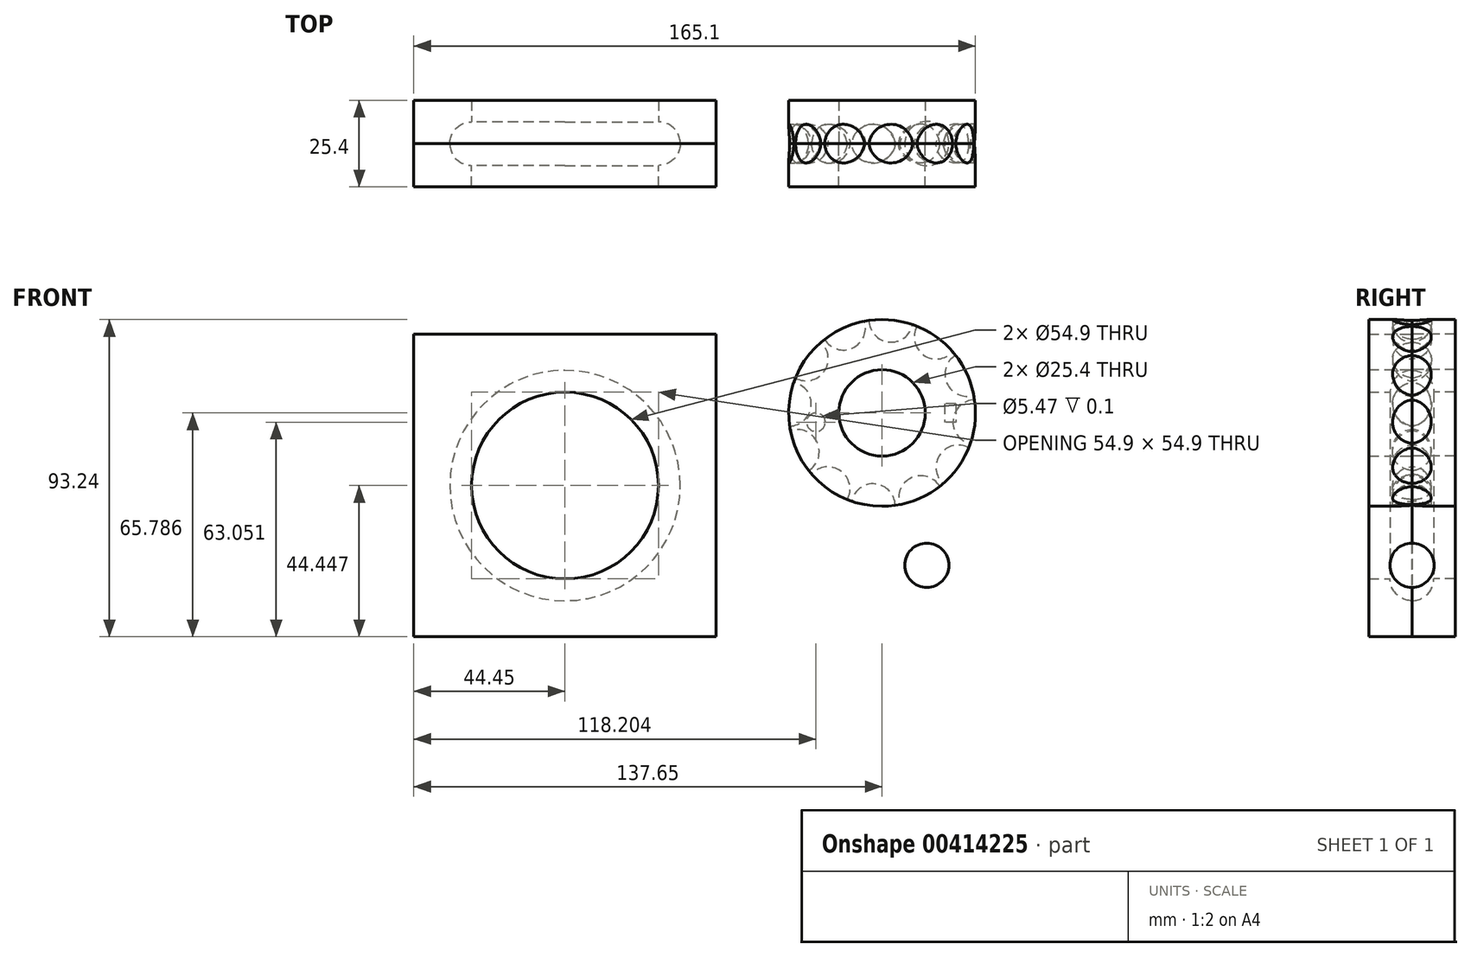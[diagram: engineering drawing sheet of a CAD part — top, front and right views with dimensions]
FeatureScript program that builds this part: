
annotation { "Feature Type Name" : "Feature", "Feature Type Description" : "" }
export const myFeature = defineFeature(function(context is Context, id is Id, definition is map)
    precondition{}
    {
        {
            var Q0;
            Q0=qCreatedBy(makeId("Front.planeOp"),FACE);
            var sketch = newSketch(context, id + "F0", { "sketchPlane" : qUnion([Q0])});
            skArc(sketch, "E0", {"start": v(0, -6.5) * mm, "mid": v(6.5, 0) * mm, "end": v(0, 6.5) * mm});
            skLineSegment(sketch, "E1", {"start": v(0, 6.5) * mm, "end": v(0, -6.5) * mm, "construction": true});
            skLineSegment(sketch, "E2", {"start": v(0, 6.5) * mm, "end": v(0, -6.5) * mm});
            skSolve(sketch);
        }
        {
            var Q0;
            Q0=makeQuery(id+"F0.imprint","IMPRINT",FACE,{"disambiguationData":[TD([[makeQuery(id+"F0.imprint","IMPRINT",EDGE,{"derivedFrom":sQuery(id+"F0.wireOp",EDGE,"E0")}),1.0]])]});
            var Q1;
            Q1=sQuery(id+"F0.wireOp",EDGE,"E2");
            revolve(context, id + "F1", {"entities" : qUnion([Q0]), "axis" : qUnion([Q1]), "revolveType" : RevolveType.FULL});
        }
        {
            var Q0;
            Q0=qCreatedBy(makeId("Front.planeOp"),FACE);
            var sketch = newSketch(context, id + "F2", { "sketchPlane" : qUnion([Q0])});
            skLineSegment(sketch, "E3.bottom", {"start": v(-150.8, 67.89) * mm, "end": v(-61.9, 67.89) * mm});
            skLineSegment(sketch, "E3.top", {"start": v(-150.8, -21.01) * mm, "end": v(-61.9, -21.01) * mm});
            skLineSegment(sketch, "E3.left", {"start": v(-150.8, 67.89) * mm, "end": v(-150.8, -21.01) * mm});
            skLineSegment(sketch, "E3.right", {"start": v(-61.9, 67.89) * mm, "end": v(-61.9, -21.01) * mm});
            skLineSegment(sketch, "E4", {"start": v(-106.35, 67.89) * mm, "end": v(-106.35, -21.01) * mm, "construction": true});
            skCircle(sketch, "E5", {"center": v(-106.35, 23.44) * mm, "radius": 20.95 * mm});
            skCircle(sketch, "E6.0", {"center": v(-106.35, 23.44) * mm, "radius": 27.45 * mm});
            skSolve(sketch);
        }
        {
            var Q0;
            Q0=sQuery(id+"F2.wireOp",EDGE,"E6.0");
            cPlane(context, id + "F3", {"entities" : qUnion([Q0]), "cplaneType" : CPlaneType.LINE_ANGLE, "offset" : 25 * mm, "angle" : 0 * degree, "width" : 150 * mm, "height" : 150 * mm});
        }
        {
            var Q0;
            Q0=qCreatedBy(id+"F3.planeOp",FACE);
            var sketch = newSketch(context, id + "F4", { "sketchPlane" : qUnion([Q0])});
            skCircle(sketch, "E7", {"center": v(-133.8, 0) * mm, "radius": 6.4 * mm});
            skSolve(sketch);
        }
        {
            var Q0;
            Q0=makeQuery(id+"F2.imprint","IMPRINT",FACE,{"disambiguationData":[TD([[makeQuery(id+"F2.imprint","IMPRINT",EDGE,{"derivedFrom":sQuery(id+"F2.wireOp",EDGE,"E3.bottom")}),-1.0]])]});
            extrude(context, id + "F5", {"entities" : qUnion([Q0]), "depth" : 12.7 * mm});
        }
        {
            var Q0;
            Q0=makeQuery(id+"F4.imprint","IMPRINT",FACE,{"disambiguationData":[TD([[makeQuery(id+"F4.imprint","IMPRINT",EDGE,{"derivedFrom":sQuery(id+"F4.wireOp",EDGE,"E7")}),1.0]])]});
            var Q1;
            Q1=sQuery(id+"F2.wireOp",EDGE,"E6.0");
            revolve(context, id + "F6", {"operationType" : NewBodyOperationType.REMOVE, "entities" : qUnion([Q0]), "axis" : qUnion([Q1]), "revolveType" : RevolveType.FULL, "oppositeDirection" : true});
        }
        {
            var Q0;
            Q0=qCreatedBy(makeId("Front.planeOp"),FACE);
            var sketch = newSketch(context, id + "F7", { "sketchPlane" : qUnion([Q0])});
            skCircle(sketch, "E8", {"center": v(-13.15, 44.78) * mm, "radius": 12.7 * mm});
            skCircle(sketch, "E9", {"center": v(-13.15, 44.78) * mm, "radius": 27.45 * mm});
            skArc(sketch, "E10", {"start": v(14.03, 48.64) * mm, "mid": v(7.7, 42.76) * mm, "end": v(12.79, 35.79) * mm});
            skLineSegment(sketch, "E11", {"start": v(14.17, 42.14) * mm, "end": v(7.7, 42.76) * mm, "construction": true});
            skLineSegment(sketch, "E12", {"start": v(7.7, 42.76) * mm, "end": v(14.17, 42.14) * mm});
            skLineSegment(sketch, "E13", {"start": v(14.03, 48.64) * mm, "end": v(12.79, 35.79) * mm});
            skArc(sketch, "E14.1.0", {"start": v(8.46, 61.7) * mm, "mid": v(5.92, 53.46) * mm, "end": v(13.8, 49.96) * mm});
            skLineSegment(sketch, "E14.1.1", {"start": v(8.46, 61.7) * mm, "end": v(13.8, 49.96) * mm});
            skArc(sketch, "E14.2.0", {"start": v(-2.9, 70.24) * mm, "mid": v(-0.98, 61.83) * mm, "end": v(7.6, 62.74) * mm});
            skLineSegment(sketch, "E14.2.1", {"start": v(-2.9, 70.24) * mm, "end": v(7.6, 62.74) * mm});
            skArc(sketch, "E14.3.0", {"start": v(-17, 71.95) * mm, "mid": v(-11.14, 65.63) * mm, "end": v(-4.16, 70.71) * mm});
            skLineSegment(sketch, "E14.3.1", {"start": v(-17, 71.95) * mm, "end": v(-4.16, 70.71) * mm});
            skArc(sketch, "E14.4.0", {"start": v(-30.08, 66.38) * mm, "mid": v(-21.83, 63.84) * mm, "end": v(-18.33, 71.73) * mm});
            skLineSegment(sketch, "E14.4.1", {"start": v(-30.08, 66.38) * mm, "end": v(-18.33, 71.73) * mm});
            skArc(sketch, "E14.5.0", {"start": v(-38.62, 55.02) * mm, "mid": v(-30.2, 56.95) * mm, "end": v(-31.12, 65.53) * mm});
            skLineSegment(sketch, "E14.5.1", {"start": v(-38.62, 55.02) * mm, "end": v(-31.12, 65.53) * mm});
            skArc(sketch, "E14.6.0", {"start": v(-40.33, 40.92) * mm, "mid": v(-34, 46.79) * mm, "end": v(-39.09, 53.77) * mm});
            skLineSegment(sketch, "E14.6.1", {"start": v(-40.33, 40.92) * mm, "end": v(-39.09, 53.77) * mm});
            skArc(sketch, "E14.7.0", {"start": v(-34.76, 27.84) * mm, "mid": v(-32.22, 36.1) * mm, "end": v(-40.1, 39.6) * mm});
            skLineSegment(sketch, "E14.7.1", {"start": v(-34.76, 27.84) * mm, "end": v(-40.1, 39.6) * mm});
            skArc(sketch, "E14.8.0", {"start": v(-23.4, 19.3) * mm, "mid": v(-25.32, 27.72) * mm, "end": v(-33.9, 26.8) * mm});
            skLineSegment(sketch, "E14.8.1", {"start": v(-23.4, 19.3) * mm, "end": v(-33.9, 26.8) * mm});
            skArc(sketch, "E14.9.0", {"start": v(-9.3, 17.6) * mm, "mid": v(-15.16, 23.92) * mm, "end": v(-22.14, 18.84) * mm});
            skLineSegment(sketch, "E14.9.1", {"start": v(-9.3, 17.6) * mm, "end": v(-22.14, 18.84) * mm});
            skArc(sketch, "E14.10.0", {"start": v(3.78, 23.17) * mm, "mid": v(-4.47, 25.7) * mm, "end": v(-7.97, 17.82) * mm});
            skLineSegment(sketch, "E14.10.1", {"start": v(3.78, 23.17) * mm, "end": v(-7.97, 17.82) * mm});
            skArc(sketch, "E14.11.0", {"start": v(12.32, 34.53) * mm, "mid": v(3.9, 32.6) * mm, "end": v(4.82, 24.02) * mm});
            skLineSegment(sketch, "E14.11.1", {"start": v(12.32, 34.53) * mm, "end": v(4.82, 24.02) * mm});
            skSolve(sketch);
        }
        {
            var Q0;
            {var subQ0=sQuery(id+"F7.wireOp",EDGE,"E10");Q0=makeQuery(id+"F7.imprint","IMPRINT",FACE,{"disambiguationData":[TD([[makeQuery(id+"F7.imprint","IMPRINT",EDGE,{"derivedFrom":subQ0}),1.0]])]});}
            var Q1;
            {var subQ1=sQuery(id+"F7.wireOp",EDGE,"E9");var subQ3=sQuery(id+"F7.wireOp",EDGE,"E12");var subQ4=makeQuery(id+"F7.imprint","INTERSECT",VERTEX,{"derivedFrom":[subQ1,subQ3]});Q1=makeQuery(id+"F7.imprint","IMPRINT",FACE,{"disambiguationData":[TD([[makeQuery(id+"F7.imprint","IMPRINT",EDGE,{"disambiguationData":[TD([[subQ4,1.0]])],"derivedFrom":subQ3}),1.0]])]});}
            var Q2;
            {var subQ1=sQuery(id+"F7.wireOp",EDGE,"E9");var subQ3=sQuery(id+"F7.wireOp",EDGE,"E12");var subQ4=makeQuery(id+"F7.imprint","INTERSECT",VERTEX,{"derivedFrom":[subQ1,subQ3]});Q2=makeQuery(id+"F7.imprint","IMPRINT",FACE,{"disambiguationData":[TD([[makeQuery(id+"F7.imprint","IMPRINT",EDGE,{"disambiguationData":[TD([[subQ4,1.0]])],"derivedFrom":subQ3}),-1.0]])]});}
            var Q3;
            {var subQ0=sQuery(id+"F7.wireOp",EDGE,"E14.1.1");Q3=makeQuery(id+"F7.imprint","IMPRINT",FACE,{"disambiguationData":[TD([[makeQuery(id+"F7.imprint","IMPRINT",EDGE,{"derivedFrom":subQ0}),1.0]])]});}
            var Q4;
            {var subQ0=sQuery(id+"F7.wireOp",EDGE,"E14.2.1");Q4=makeQuery(id+"F7.imprint","IMPRINT",FACE,{"disambiguationData":[TD([[makeQuery(id+"F7.imprint","IMPRINT",EDGE,{"derivedFrom":subQ0}),1.0]])]});}
            var Q5;
            Q5=makeQuery(id+"F7.imprint","IMPRINT",FACE,{"disambiguationData":[TD([[makeQuery(id+"F7.imprint","IMPRINT",EDGE,{"derivedFrom":sQuery(id+"F7.wireOp",EDGE,"E14.1.0")}),1.0]])]});
            var Q6;
            Q6=makeQuery(id+"F7.imprint","IMPRINT",FACE,{"disambiguationData":[TD([[makeQuery(id+"F7.imprint","IMPRINT",EDGE,{"derivedFrom":sQuery(id+"F7.wireOp",EDGE,"E14.2.0")}),1.0]])]});
            var Q7;
            Q7=makeQuery(id+"F7.imprint","IMPRINT",FACE,{"disambiguationData":[TD([[makeQuery(id+"F7.imprint","IMPRINT",EDGE,{"derivedFrom":sQuery(id+"F7.wireOp",EDGE,"E14.3.0")}),1.0]])]});
            var Q8;
            Q8=makeQuery(id+"F7.imprint","IMPRINT",FACE,{"disambiguationData":[TD([[makeQuery(id+"F7.imprint","IMPRINT",EDGE,{"derivedFrom":sQuery(id+"F7.wireOp",EDGE,"E14.4.0")}),1.0]])]});
            var Q9;
            Q9=makeQuery(id+"F7.imprint","IMPRINT",FACE,{"disambiguationData":[TD([[makeQuery(id+"F7.imprint","IMPRINT",EDGE,{"derivedFrom":sQuery(id+"F7.wireOp",EDGE,"E14.5.0")}),1.0]])]});
            var Q10;
            Q10=makeQuery(id+"F7.imprint","IMPRINT",FACE,{"disambiguationData":[TD([[makeQuery(id+"F7.imprint","IMPRINT",EDGE,{"derivedFrom":sQuery(id+"F7.wireOp",EDGE,"E8")}),-1.0]])]});
            var Q11;
            Q11=makeQuery(id+"F7.imprint","IMPRINT",FACE,{"disambiguationData":[TD([[makeQuery(id+"F7.imprint","IMPRINT",EDGE,{"derivedFrom":sQuery(id+"F7.wireOp",EDGE,"E14.11.0")}),1.0]])]});
            var Q12;
            Q12=makeQuery(id+"F7.imprint","IMPRINT",FACE,{"disambiguationData":[TD([[makeQuery(id+"F7.imprint","IMPRINT",EDGE,{"derivedFrom":sQuery(id+"F7.wireOp",EDGE,"E14.10.0")}),1.0]])]});
            var Q13;
            Q13=makeQuery(id+"F7.imprint","IMPRINT",FACE,{"disambiguationData":[TD([[makeQuery(id+"F7.imprint","IMPRINT",EDGE,{"derivedFrom":sQuery(id+"F7.wireOp",EDGE,"E14.9.0")}),1.0]])]});
            var Q14;
            Q14=makeQuery(id+"F7.imprint","IMPRINT",FACE,{"disambiguationData":[TD([[makeQuery(id+"F7.imprint","IMPRINT",EDGE,{"derivedFrom":sQuery(id+"F7.wireOp",EDGE,"E14.8.0")}),1.0]])]});
            var Q15;
            Q15=makeQuery(id+"F7.imprint","IMPRINT",FACE,{"disambiguationData":[TD([[makeQuery(id+"F7.imprint","IMPRINT",EDGE,{"derivedFrom":sQuery(id+"F7.wireOp",EDGE,"E14.7.0")}),1.0]])]});
            var Q16;
            Q16=makeQuery(id+"F7.imprint","IMPRINT",FACE,{"disambiguationData":[TD([[makeQuery(id+"F7.imprint","IMPRINT",EDGE,{"derivedFrom":sQuery(id+"F7.wireOp",EDGE,"E14.6.0")}),1.0]])]});
            var Q17;
            {var subQ0=sQuery(id+"F7.wireOp",EDGE,"E14.4.1");Q17=makeQuery(id+"F7.imprint","IMPRINT",FACE,{"disambiguationData":[TD([[makeQuery(id+"F7.imprint","IMPRINT",EDGE,{"derivedFrom":subQ0}),1.0]])]});}
            var Q18;
            {var subQ0=sQuery(id+"F7.wireOp",EDGE,"E14.5.1");Q18=makeQuery(id+"F7.imprint","IMPRINT",FACE,{"disambiguationData":[TD([[makeQuery(id+"F7.imprint","IMPRINT",EDGE,{"derivedFrom":subQ0}),1.0]])]});}
            var Q19;
            {var subQ0=sQuery(id+"F7.wireOp",EDGE,"E14.3.1");Q19=makeQuery(id+"F7.imprint","IMPRINT",FACE,{"disambiguationData":[TD([[makeQuery(id+"F7.imprint","IMPRINT",EDGE,{"derivedFrom":subQ0}),1.0]])]});}
            var Q20;
            {var subQ0=sQuery(id+"F7.wireOp",EDGE,"E14.6.1");Q20=makeQuery(id+"F7.imprint","IMPRINT",FACE,{"disambiguationData":[TD([[makeQuery(id+"F7.imprint","IMPRINT",EDGE,{"derivedFrom":subQ0}),1.0]])]});}
            var Q21;
            {var subQ0=sQuery(id+"F7.wireOp",EDGE,"E14.7.1");Q21=makeQuery(id+"F7.imprint","IMPRINT",FACE,{"disambiguationData":[TD([[makeQuery(id+"F7.imprint","IMPRINT",EDGE,{"derivedFrom":subQ0}),1.0]])]});}
            var Q22;
            {var subQ0=sQuery(id+"F7.wireOp",EDGE,"E14.8.1");Q22=makeQuery(id+"F7.imprint","IMPRINT",FACE,{"disambiguationData":[TD([[makeQuery(id+"F7.imprint","IMPRINT",EDGE,{"derivedFrom":subQ0}),1.0]])]});}
            var Q23;
            {var subQ0=sQuery(id+"F7.wireOp",EDGE,"E14.9.1");Q23=makeQuery(id+"F7.imprint","IMPRINT",FACE,{"disambiguationData":[TD([[makeQuery(id+"F7.imprint","IMPRINT",EDGE,{"derivedFrom":subQ0}),1.0]])]});}
            var Q24;
            {var subQ0=sQuery(id+"F7.wireOp",EDGE,"E14.10.1");Q24=makeQuery(id+"F7.imprint","IMPRINT",FACE,{"disambiguationData":[TD([[makeQuery(id+"F7.imprint","IMPRINT",EDGE,{"derivedFrom":subQ0}),1.0]])]});}
            var Q25;
            {var subQ0=sQuery(id+"F7.wireOp",EDGE,"E14.11.1");Q25=makeQuery(id+"F7.imprint","IMPRINT",FACE,{"disambiguationData":[TD([[makeQuery(id+"F7.imprint","IMPRINT",EDGE,{"derivedFrom":subQ0}),1.0]])]});}
            extrude(context, id + "F8", {"entities" : qUnion([Q0, Q1, Q2, Q3, Q4, Q5, Q6, Q7, Q8, Q9, Q10, Q11, Q12, Q13, Q14, Q15, Q16, Q17, Q18, Q19, Q20, Q21, Q22, Q23, Q24, Q25]), "depth" : 12.7 * mm});
        }
        {
            var Q0;
            {var subQ1=sQuery(id+"F7.wireOp",EDGE,"E10");var subQ3=sQuery(id+"F7.wireOp",EDGE,"E12");var subQ4=makeQuery(id+"F7.imprint","INTERSECT",VERTEX,{"derivedFrom":[subQ1,subQ3]});Q0=makeQuery(id+"F7.imprint","IMPRINT",FACE,{"disambiguationData":[TD([[makeQuery(id+"F7.imprint","IMPRINT",EDGE,{"disambiguationData":[TD([[subQ4,-1.0]])],"derivedFrom":subQ3}),1.0]])]});}
            var Q1;
            {var subQ1=sQuery(id+"F7.wireOp",EDGE,"E10");var subQ3=sQuery(id+"F7.wireOp",EDGE,"E12");var subQ4=makeQuery(id+"F7.imprint","INTERSECT",VERTEX,{"derivedFrom":[subQ1,subQ3]});Q1=makeQuery(id+"F7.imprint","IMPRINT",FACE,{"disambiguationData":[TD([[makeQuery(id+"F7.imprint","IMPRINT",EDGE,{"disambiguationData":[TD([[subQ4,-1.0]])],"derivedFrom":subQ3}),-1.0]])]});}
            var Q2;
            Q2=sQuery(id+"F7.wireOp",EDGE,"E13");
            revolve(context, id + "F9", {"operationType" : NewBodyOperationType.REMOVE, "entities" : qUnion([Q0, Q1]), "axis" : qUnion([Q2]), "revolveType" : RevolveType.FULL, "oppositeDirection" : true});
        }
        {
            var Q0;
            Q0=makeQuery(id+"F7.imprint","IMPRINT",FACE,{"disambiguationData":[TD([[makeQuery(id+"F7.imprint","IMPRINT",EDGE,{"derivedFrom":sQuery(id+"F7.wireOp",EDGE,"E14.1.0")}),1.0]])]});
            var Q1;
            Q1=sQuery(id+"F7.wireOp",EDGE,"E14.1.1");
            revolve(context, id + "F10", {"operationType" : NewBodyOperationType.REMOVE, "entities" : qUnion([Q0]), "axis" : qUnion([Q1]), "revolveType" : RevolveType.FULL, "oppositeDirection" : true});
        }
        {
            var Q0;
            Q0=makeQuery(id+"F7.imprint","IMPRINT",FACE,{"disambiguationData":[TD([[makeQuery(id+"F7.imprint","IMPRINT",EDGE,{"derivedFrom":sQuery(id+"F7.wireOp",EDGE,"E14.2.0")}),1.0]])]});
            var Q1;
            Q1=sQuery(id+"F7.wireOp",EDGE,"E14.2.1");
            revolve(context, id + "F11", {"operationType" : NewBodyOperationType.REMOVE, "entities" : qUnion([Q0]), "axis" : qUnion([Q1]), "revolveType" : RevolveType.FULL, "oppositeDirection" : true});
        }
        {
            var Q0;
            Q0=makeQuery(id+"F7.imprint","IMPRINT",FACE,{"disambiguationData":[TD([[makeQuery(id+"F7.imprint","IMPRINT",EDGE,{"derivedFrom":sQuery(id+"F7.wireOp",EDGE,"E14.3.0")}),1.0]])]});
            var Q1;
            Q1=sQuery(id+"F7.wireOp",EDGE,"E14.3.1");
            revolve(context, id + "F12", {"operationType" : NewBodyOperationType.REMOVE, "entities" : qUnion([Q0]), "axis" : qUnion([Q1]), "revolveType" : RevolveType.FULL, "oppositeDirection" : true});
        }
        {
            var Q0;
            Q0=makeQuery(id+"F7.imprint","IMPRINT",FACE,{"disambiguationData":[TD([[makeQuery(id+"F7.imprint","IMPRINT",EDGE,{"derivedFrom":sQuery(id+"F7.wireOp",EDGE,"E14.4.0")}),1.0]])]});
            var Q1;
            Q1=sQuery(id+"F7.wireOp",EDGE,"E14.4.1");
            revolve(context, id + "F13", {"operationType" : NewBodyOperationType.REMOVE, "entities" : qUnion([Q0]), "axis" : qUnion([Q1]), "revolveType" : RevolveType.FULL, "oppositeDirection" : true});
        }
        {
            var Q0;
            Q0=makeQuery(id+"F7.imprint","IMPRINT",FACE,{"disambiguationData":[TD([[makeQuery(id+"F7.imprint","IMPRINT",EDGE,{"derivedFrom":sQuery(id+"F7.wireOp",EDGE,"E14.5.0")}),1.0]])]});
            var Q1;
            Q1=sQuery(id+"F7.wireOp",EDGE,"E14.5.1");
            revolve(context, id + "F14", {"operationType" : NewBodyOperationType.REMOVE, "entities" : qUnion([Q0]), "axis" : qUnion([Q1]), "revolveType" : RevolveType.FULL, "oppositeDirection" : true});
        }
        {
            var Q0;
            Q0=makeQuery(id+"F7.imprint","IMPRINT",FACE,{"disambiguationData":[TD([[makeQuery(id+"F7.imprint","IMPRINT",EDGE,{"derivedFrom":sQuery(id+"F7.wireOp",EDGE,"E14.6.0")}),1.0]])]});
            var Q1;
            Q1=sQuery(id+"F7.wireOp",EDGE,"E14.6.1");
            revolve(context, id + "F15", {"operationType" : NewBodyOperationType.REMOVE, "entities" : qUnion([Q0]), "axis" : qUnion([Q1]), "revolveType" : RevolveType.FULL, "oppositeDirection" : true});
        }
        {
            var Q0;
            Q0=makeQuery(id+"F7.imprint","IMPRINT",FACE,{"disambiguationData":[TD([[makeQuery(id+"F7.imprint","IMPRINT",EDGE,{"derivedFrom":sQuery(id+"F7.wireOp",EDGE,"E14.7.0")}),1.0]])]});
            var Q1;
            Q1=sQuery(id+"F7.wireOp",EDGE,"E14.7.1");
            revolve(context, id + "F16", {"operationType" : NewBodyOperationType.REMOVE, "entities" : qUnion([Q0]), "axis" : qUnion([Q1]), "revolveType" : RevolveType.FULL, "oppositeDirection" : true});
        }
        {
            var Q0;
            Q0=makeQuery(id+"F7.imprint","IMPRINT",FACE,{"disambiguationData":[TD([[makeQuery(id+"F7.imprint","IMPRINT",EDGE,{"derivedFrom":sQuery(id+"F7.wireOp",EDGE,"E14.8.0")}),1.0]])]});
            var Q1;
            Q1=sQuery(id+"F7.wireOp",EDGE,"E14.8.1");
            revolve(context, id + "F17", {"operationType" : NewBodyOperationType.REMOVE, "entities" : qUnion([Q0]), "axis" : qUnion([Q1]), "revolveType" : RevolveType.FULL, "oppositeDirection" : true});
        }
        {
            var Q0;
            Q0=makeQuery(id+"F7.imprint","IMPRINT",FACE,{"disambiguationData":[TD([[makeQuery(id+"F7.imprint","IMPRINT",EDGE,{"derivedFrom":sQuery(id+"F7.wireOp",EDGE,"E14.9.0")}),1.0]])]});
            var Q1;
            Q1=sQuery(id+"F7.wireOp",EDGE,"E14.9.1");
            revolve(context, id + "F18", {"operationType" : NewBodyOperationType.REMOVE, "entities" : qUnion([Q0]), "axis" : qUnion([Q1]), "revolveType" : RevolveType.FULL, "oppositeDirection" : true});
        }
        {
            var Q0;
            Q0=makeQuery(id+"F7.imprint","IMPRINT",FACE,{"disambiguationData":[TD([[makeQuery(id+"F7.imprint","IMPRINT",EDGE,{"derivedFrom":sQuery(id+"F7.wireOp",EDGE,"E14.10.0")}),1.0]])]});
            var Q1;
            Q1=sQuery(id+"F7.wireOp",EDGE,"E14.10.1");
            revolve(context, id + "F19", {"operationType" : NewBodyOperationType.REMOVE, "entities" : qUnion([Q0]), "axis" : qUnion([Q1]), "revolveType" : RevolveType.FULL, "oppositeDirection" : true});
        }
        {
            var Q0;
            Q0=makeQuery(id+"F7.imprint","IMPRINT",FACE,{"disambiguationData":[TD([[makeQuery(id+"F7.imprint","IMPRINT",EDGE,{"derivedFrom":sQuery(id+"F7.wireOp",EDGE,"E14.11.0")}),1.0]])]});
            var Q1;
            Q1=sQuery(id+"F7.wireOp",EDGE,"E14.11.1");
            revolve(context, id + "F20", {"operationType" : NewBodyOperationType.REMOVE, "entities" : qUnion([Q0]), "axis" : qUnion([Q1]), "revolveType" : RevolveType.FULL, "oppositeDirection" : true});
        }
        {
            var Q0;
            Q0=makeQuery(id+"F8.opExtrude","SWEPT_BODY",BODY,{"disambiguationData":[OSD([sQuery(id+"F7.wireOp",EDGE,"E8"),sQuery(id+"F7.wireOp",EDGE,"E9")])]});
            var Q1;
            Q1=makeQuery(id+"F8.opExtrude","CAP_FACE",FACE,{"disambiguationData":[OSD([sQuery(id+"F7.wireOp",EDGE,"E8"),sQuery(id+"F7.wireOp",EDGE,"E9")])],"isStart":true});
            mirror(context, id + "F21", {"operationType" : NewBodyOperationType.ADD, "entities" : qUnion([Q0]), "mirrorPlane" : qUnion([Q1])});
        }
        {
            var Q0;
            Q0=makeQuery(id+"F21.opPattern","COPY",FACE,{"derivedFrom":makeQuery(id+"F8.opExtrude","CAP_FACE",FACE,{"disambiguationData":[OSD([sQuery(id+"F7.wireOp",EDGE,"E8"),sQuery(id+"F7.wireOp",EDGE,"E9")])],"isStart":false}),"instanceName":"1"});
            var sketch = newSketch(context, id + "F22", { "sketchPlane" : qUnion([Q0])});
            skCircle(sketch, "E15", {"center": v(32.6, 42.04) * mm, "radius": 2.73 * mm});
            skLineSegment(sketch, "E16.bottom", {"start": v(-8.55, 47.43) * mm, "end": v(-5.27, 47.43) * mm});
            skLineSegment(sketch, "E16.top", {"start": v(-8.55, 42) * mm, "end": v(-5.27, 42) * mm});
            skLineSegment(sketch, "E16.left", {"start": v(-8.55, 47.43) * mm, "end": v(-8.55, 42) * mm});
            skLineSegment(sketch, "E16.right", {"start": v(-5.27, 47.43) * mm, "end": v(-5.27, 42) * mm});
            skSolve(sketch);
        }
        {
            var Q0;
            Q0=makeQuery(id+"F22.imprint","IMPRINT",FACE,{"disambiguationData":[TD([[makeQuery(id+"F22.imprint","IMPRINT",EDGE,{"derivedFrom":sQuery(id+"F22.wireOp",EDGE,"E16.bottom")}),-1.0]])]});
            extrude(context, id + "F23", {"entities" : qUnion([Q0]), "operationType" : NewBodyOperationType.REMOVE, "oppositeDirection" : true, "depth" : 0.1 * mm});
        }
        {
            var Q0;
            Q0=makeQuery(id+"F22.imprint","IMPRINT",FACE,{"disambiguationData":[TD([[makeQuery(id+"F22.imprint","IMPRINT",EDGE,{"derivedFrom":sQuery(id+"F22.wireOp",EDGE,"E15")}),1.0]])]});
            extrude(context, id + "F24", {"entities" : qUnion([Q0]), "operationType" : NewBodyOperationType.REMOVE, "oppositeDirection" : true, "depth" : 0.1 * mm});
        }
        {
            var Q0;
            Q0=makeQuery(id+"F5.opExtrude","SWEPT_BODY",BODY,{"disambiguationData":[OSD([sQuery(id+"F2.wireOp",EDGE,"E3.bottom"),sQuery(id+"F2.wireOp",EDGE,"E3.top"),sQuery(id+"F2.wireOp",EDGE,"E3.left"),sQuery(id+"F2.wireOp",EDGE,"E3.right"),sQuery(id+"F2.wireOp",EDGE,"E6.0")])]});
            var Q1;
            Q1=makeQuery(id+"F2.imprint","IMPRINT",FACE,{"disambiguationData":[TD([[makeQuery(id+"F2.imprint","IMPRINT",EDGE,{"derivedFrom":sQuery(id+"F2.wireOp",EDGE,"E3.bottom")}),-1.0]])]});
            mirror(context, id + "F25", {"operationType" : NewBodyOperationType.ADD, "entities" : qUnion([Q0]), "mirrorPlane" : qUnion([Q1])});
        }
    });
